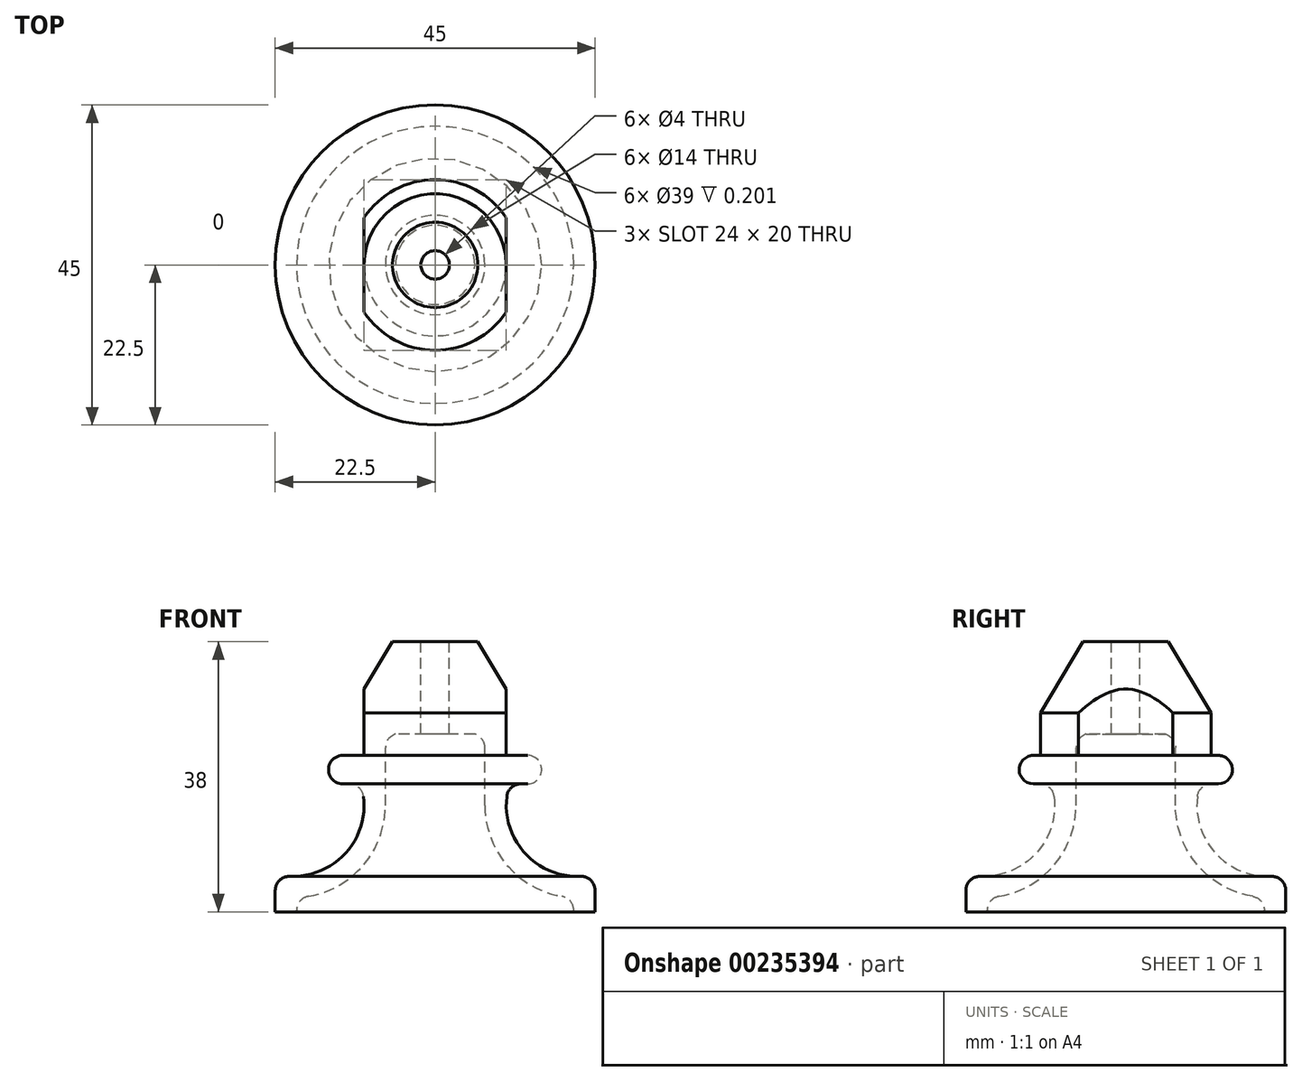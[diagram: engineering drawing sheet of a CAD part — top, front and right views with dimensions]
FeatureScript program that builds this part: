
annotation { "Feature Type Name" : "Feature", "Feature Type Description" : "" }
export const myFeature = defineFeature(function(context is Context, id is Id, definition is map)
    precondition{}
    {
        {
            var Q0;
            Q0=qCreatedBy(makeId("Front.planeOp"),FACE);
            var sketch = newSketch(context, id + "F0", { "sketchPlane" : qUnion([Q0])});
            skLineSegment(sketch, "E0", {"start": v(22.5, 0) * mm, "end": v(22.5, 3) * mm});
            skLineSegment(sketch, "E1", {"start": v(22.5, 0) * mm, "end": v(19.5, 0) * mm});
            skPoint(sketch, "E2.end.orphan", {"position": v(0, -82.76) * mm});
            skArc(sketch, "E3", {"start": v(10.08, 16.25) * mm, "mid": v(12.64, 8.23) * mm, "end": v(20.42, 5) * mm});
            skPoint(sketch, "E4.visualSharp", {"position": v(22.5, 5.3) * mm});
            skArc(sketch, "E4.filletArc", {"start": v(22.5, 3) * mm, "mid": v(21.88, 4.45) * mm, "end": v(20.42, 5) * mm});
            skLineSegment(sketch, "E5.bottom", {"start": v(12.06, 18) * mm, "end": v(13, 18) * mm});
            skLineSegment(sketch, "E5.top", {"start": v(12, 22) * mm, "end": v(13, 22) * mm});
            skLineSegment(sketch, "E5.right", {"start": v(15, 20) * mm, "end": v(15, 20) * mm});
            skPoint(sketch, "E6.visualSharp", {"position": v(15, 22) * mm});
            skArc(sketch, "E6.filletArc", {"start": v(15, 20) * mm, "mid": v(14.41, 21.41) * mm, "end": v(13, 22) * mm});
            skPoint(sketch, "E7.visualSharp", {"position": v(15, 18) * mm});
            skArc(sketch, "E7.filletArc", {"start": v(13, 18) * mm, "mid": v(14.41, 18.59) * mm, "end": v(15, 20) * mm});
            skLineSegment(sketch, "E8", {"start": v(12, 22) * mm, "end": v(12, 28) * mm});
            skLineSegment(sketch, "E9", {"start": v(12, 28) * mm, "end": v(6, 38) * mm});
            skLineSegment(sketch, "E10", {"start": v(7, 23.08) * mm, "end": v(7, 15) * mm});
            skPoint(sketch, "E11.visualSharp", {"position": v(7, 25) * mm});
            skArc(sketch, "E11.filletArc", {"start": v(7, 23.08) * mm, "mid": v(6.6, 24.28) * mm, "end": v(5.58, 25) * mm});
            skArc(sketch, "E12.0", {"start": v(7, 15) * mm, "mid": v(10.07, 6.6) * mm, "end": v(17.83, 2.17) * mm});
            skLineSegment(sketch, "E13", {"start": v(0, -12.17) * mm, "end": v(0, -101.63) * mm, "construction": true});
            skLineSegment(sketch, "E14", {"start": v(19.5, 0.2) * mm, "end": v(19.5, 0) * mm});
            skLineSegment(sketch, "E15", {"start": v(6, 38) * mm, "end": v(0, 38) * mm});
            skLineSegment(sketch, "E16", {"start": v(5.58, 25) * mm, "end": v(0, 25) * mm});
            skLineSegment(sketch, "E17", {"start": v(0, 38) * mm, "end": v(0, 25) * mm});
            skLineSegment(sketch, "E18", {"start": v(2, 38) * mm, "end": v(2, 25) * mm});
            skLineSegment(sketch, "E19", {"start": v(0, 0) * mm, "end": v(19.5, 0) * mm, "construction": true});
            skPoint(sketch, "E20.visualSharp", {"position": v(10.46, 18) * mm});
            skArc(sketch, "E20.filletArc", {"start": v(12.06, 18) * mm, "mid": v(10.74, 17.5) * mm, "end": v(10.08, 16.25) * mm});
            skPoint(sketch, "E21.visualSharp", {"position": v(19.5, 2) * mm});
            skArc(sketch, "E21.filletArc", {"start": v(19.5, 0.2) * mm, "mid": v(19.03, 1.5) * mm, "end": v(17.83, 2.17) * mm});
            skSolve(sketch);
        }
        {
            var Q0;
            Q0=makeQuery(id+"F0.imprint","IMPRINT",FACE,{"disambiguationData":[TD([[makeQuery(id+"F0.imprint","IMPRINT",EDGE,{"derivedFrom":sQuery(id+"F0.wireOp",EDGE,"E0")}),1.0]])]});
            var Q1;
            Q1=sQuery(id+"F0.wireOp",EDGE,"E17");
            revolve(context, id + "F1", {"entities" : qUnion([Q0]), "axis" : qUnion([Q1]), "revolveType" : RevolveType.FULL});
        }
        {
            var Q0;
            Q0=makeQuery(id+"F1.opRevolve","SWEPT_FACE",FACE,{"disambiguationData":[OSD([sQuery(id+"F0.wireOp",EDGE,"E15")])]});
            var sketch = newSketch(context, id + "F2", { "sketchPlane" : qUnion([Q0])});
            skCircle(sketch, "E22.0", {"center": v(0, 0) * mm, "radius": 12 * mm});
            skLineSegment(sketch, "E23.bottom", {"start": v(10, 6.63) * mm, "end": v(-10, 6.63) * mm});
            skLineSegment(sketch, "E23.top", {"start": v(10, -6.63) * mm, "end": v(-10, -6.63) * mm});
            skLineSegment(sketch, "E23.left", {"start": v(10, 6.63) * mm, "end": v(10, -6.63) * mm});
            skLineSegment(sketch, "E23.right", {"start": v(-10, 6.63) * mm, "end": v(-10, -6.63) * mm});
            skSolve(sketch);
        }
        {
            var Q0;
            {var subQ0=sQuery(id+"F2.wireOp",EDGE,"E23.left");Q0=makeQuery(id+"F2.imprint","IMPRINT",FACE,{"disambiguationData":[TD([[makeQuery(id+"F2.imprint","IMPRINT",EDGE,{"derivedFrom":subQ0}),1.0]])]});}
            var Q1;
            {var subQ0=sQuery(id+"F2.wireOp",EDGE,"E23.right");Q1=makeQuery(id+"F2.imprint","IMPRINT",FACE,{"disambiguationData":[TD([[makeQuery(id+"F2.imprint","IMPRINT",EDGE,{"derivedFrom":subQ0}),-1.0]])]});}
            var Q2;
            Q2=makeQuery(id+"F1.opRevolve","SWEPT_FACE",FACE,{"disambiguationData":[OSD([sQuery(id+"F0.wireOp",EDGE,"E5.top")])]});
            extrude(context, id + "F3", {"entities" : qUnion([Q0, Q1]), "operationType" : NewBodyOperationType.REMOVE, "endBound" : BoundingType.UP_TO_SURFACE, "oppositeDirection" : true, "endBoundEntityFace" : qUnion([Q2]), "depth" : 25 * mm});
        }
    });
